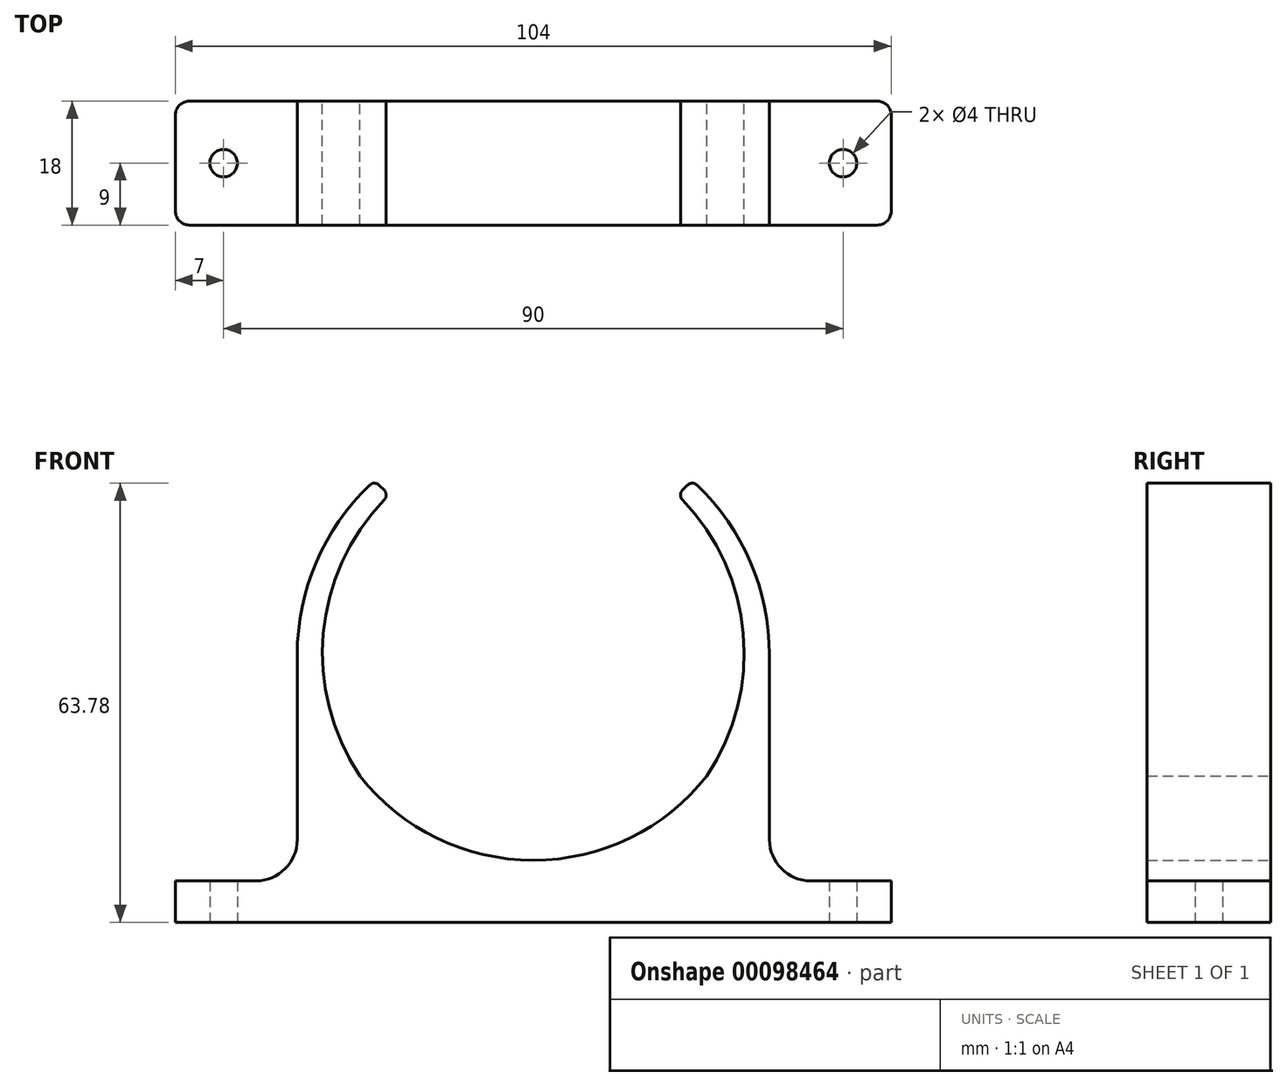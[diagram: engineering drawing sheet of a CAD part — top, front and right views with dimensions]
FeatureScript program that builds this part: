
annotation { "Feature Type Name" : "Feature", "Feature Type Description" : "" }
export const myFeature = defineFeature(function(context is Context, id is Id, definition is map)
    precondition{}
    {
        {
            var Q0;
            Q0=qCreatedBy(makeId("Front.planeOp"),FACE);
            var sketch = newSketch(context, id + "F0", { "sketchPlane" : qUnion([Q0])});
            skArc(sketch, "E0", {"start": v(-25.21, -19.87) * mm, "mid": v(0, -32.1) * mm, "end": v(25.21, -19.87) * mm});
            skCircle(sketch, "E1.0", {"center": v(0, 0) * mm, "radius": 34.1 * mm, "construction": true});
            skCircle(sketch, "E2.0", {"center": v(0, 0) * mm, "radius": 30.1 * mm, "construction": true});
            skArc(sketch, "E3", {"start": v(25.21, -19.87) * mm, "mid": v(30.51, 0.83) * mm, "end": v(21.66, 20.28) * mm});
            skLineSegment(sketch, "E4", {"start": v(20.97, 20.97) * mm, "end": v(21.28, 21.28) * mm, "construction": true});
            skPoint(sketch, "E5.orphan", {"position": v(0, 30.1) * mm});
            skLineSegment(sketch, "E6", {"start": v(34.3, -35.1) * mm, "end": v(52, -35.1) * mm});
            skLineSegment(sketch, "E7", {"start": v(52, -35.1) * mm, "end": v(52, -41.1) * mm});
            skLineSegment(sketch, "E8", {"start": v(52, -41.1) * mm, "end": v(0, -41.1) * mm});
            skLineSegment(sketch, "E9", {"start": v(34.3, -2.24) * mm, "end": v(34.3, -35.1) * mm});
            skArc(sketch, "E10.trimOffspring", {"start": v(34.3, -2.24) * mm, "mid": v(31.56, 11.16) * mm, "end": v(23.78, 22.4) * mm});
            skPoint(sketch, "E11.visualSharp", {"position": v(20.97, 20.97) * mm});
            skArc(sketch, "E11.filletArc", {"start": v(21.68, 21.68) * mm, "mid": v(21.38, 20.98) * mm, "end": v(21.66, 20.28) * mm});
            skPoint(sketch, "E12.visualSharp", {"position": v(23.07, 23.07) * mm});
            skArc(sketch, "E12.filletArc", {"start": v(23.78, 22.4) * mm, "mid": v(23.08, 22.68) * mm, "end": v(22.38, 22.38) * mm});
            skLineSegment(sketch, "E13", {"start": v(21.68, 21.68) * mm, "end": v(22.38, 22.38) * mm});
            skPoint(sketch, "E14.orphan", {"position": v(33.96, -7.02) * mm});
            skPoint(sketch, "E15.MirrorCS.end.orphan", {"position": v(0, -41.1) * mm});
            skPoint(sketch, "E16.MirrorCS.start.orphan", {"position": v(0, -34.1) * mm});
            skArc(sketch, "E17.MirrorCS", {"start": v(-25.21, -19.87) * mm, "mid": v(-30.51, 0.83) * mm, "end": v(-21.66, 20.28) * mm});
            skArc(sketch, "E18.MirrorCS", {"start": v(-21.68, 21.68) * mm, "mid": v(-21.38, 20.98) * mm, "end": v(-21.66, 20.28) * mm});
            skLineSegment(sketch, "E19.MirrorCS", {"start": v(-21.68, 21.68) * mm, "end": v(-22.38, 22.38) * mm});
            skArc(sketch, "E20.MirrorCS", {"start": v(-23.78, 22.4) * mm, "mid": v(-23.08, 22.68) * mm, "end": v(-22.38, 22.38) * mm});
            skArc(sketch, "E21.MirrorCS", {"start": v(-34.3, -2.24) * mm, "mid": v(-31.56, 11.16) * mm, "end": v(-23.78, 22.4) * mm});
            skLineSegment(sketch, "E22.MirrorCS", {"start": v(-34.3, -2.24) * mm, "end": v(-34.3, -35.1) * mm});
            skLineSegment(sketch, "E23.MirrorCS", {"start": v(-34.3, -35.1) * mm, "end": v(-52, -35.1) * mm});
            skLineSegment(sketch, "E24.MirrorCS", {"start": v(-52, -35.1) * mm, "end": v(-52, -41.1) * mm});
            skLineSegment(sketch, "E25.MirrorCS", {"start": v(-52, -41.1) * mm, "end": v(0, -41.1) * mm});
            skArc(sketch, "E26.trimOffspring", {"start": v(22.77, 22.62) * mm, "mid": v(0, 32.1) * mm, "end": v(-22.77, 22.62) * mm});
            skSolve(sketch);
        }
        {
            var Q0;
            Q0=makeQuery(id+"F0.imprint","IMPRINT",FACE,{"disambiguationData":[TD([[makeQuery(id+"F0.imprint","IMPRINT",EDGE,{"derivedFrom":sQuery(id+"F0.wireOp",EDGE,"E0")}),-1.0]])]});
            extrude(context, id + "F1", {"entities" : qUnion([Q0]), "depth" : 18 * mm});
        }
        {
            var Q0;
            Q0=makeQuery(id+"F1.opExtrude","SWEPT_FACE",FACE,{"disambiguationData":[OSD([sQuery(id+"F0.wireOp",EDGE,"E8"),sQuery(id+"F0.wireOp",EDGE,"E15.MirrorCS")])]});
            var sketch = newSketch(context, id + "F2", { "sketchPlane" : qUnion([Q0])});
            skLineSegment(sketch, "E27", {"start": v(52, 9) * mm, "end": v(-48, 9) * mm, "construction": true});
            skCircle(sketch, "E28", {"center": v(-45, 9) * mm, "radius": 2 * mm});
            skCircle(sketch, "E29.MirrorC", {"center": v(45, 9) * mm, "radius": 2 * mm});
            skSolve(sketch);
        }
        {
            var Q0;
            Q0=qSketchRegion(id+"F2",true);
            extrude(context, id + "F3", {"entities" : qUnion([Q0]), "operationType" : NewBodyOperationType.REMOVE, "endBound" : BoundingType.UP_TO_NEXT, "oppositeDirection" : true, "depth" : 25 * mm});
        }
        {
            var Q0;
            Q0=makeQuery(id+"F1.opExtrude","CAP_EDGE",EDGE,{"disambiguationData":[OSD([sQuery(id+"F0.wireOp",EDGE,"E24.MirrorCS")])],"isStart":true});
            var Q1;
            Q1=makeQuery(id+"F1.opExtrude","CAP_EDGE",EDGE,{"disambiguationData":[OSD([sQuery(id+"F0.wireOp",EDGE,"E24.MirrorCS")])],"isStart":false});
            var Q2;
            Q2=makeQuery(id+"F1.opExtrude","CAP_EDGE",EDGE,{"disambiguationData":[OSD([sQuery(id+"F0.wireOp",EDGE,"E7")])],"isStart":false});
            var Q3;
            Q3=makeQuery(id+"F1.opExtrude","CAP_EDGE",EDGE,{"disambiguationData":[OSD([sQuery(id+"F0.wireOp",EDGE,"E7")])],"isStart":true});
            fillet(context, id + "F4", {"entities" : qUnion([Q0, Q1, Q2, Q3]), "radius" : 2 * mm, "tangentPropagation" : true, "allowEdgeOverflow" : false});
        }
        {
            var Q0;
            Q0=makeQuery(id+"F1.opExtrude","SWEPT_EDGE",EDGE,{"disambiguationData":[OSD([sQuery(id+"F0.wireOp",EDGE,"E22.MirrorCS"),sQuery(id+"F0.wireOp",EDGE,"E23.MirrorCS")])]});
            var Q1;
            Q1=makeQuery(id+"F1.opExtrude","SWEPT_EDGE",EDGE,{"disambiguationData":[OSD([sQuery(id+"F0.wireOp",EDGE,"E6"),sQuery(id+"F0.wireOp",EDGE,"E9")])]});
            fillet(context, id + "F5", {"entities" : qUnion([Q0, Q1]), "radius" : 6 * mm, "tangentPropagation" : true, "allowEdgeOverflow" : false});
        }
    });
